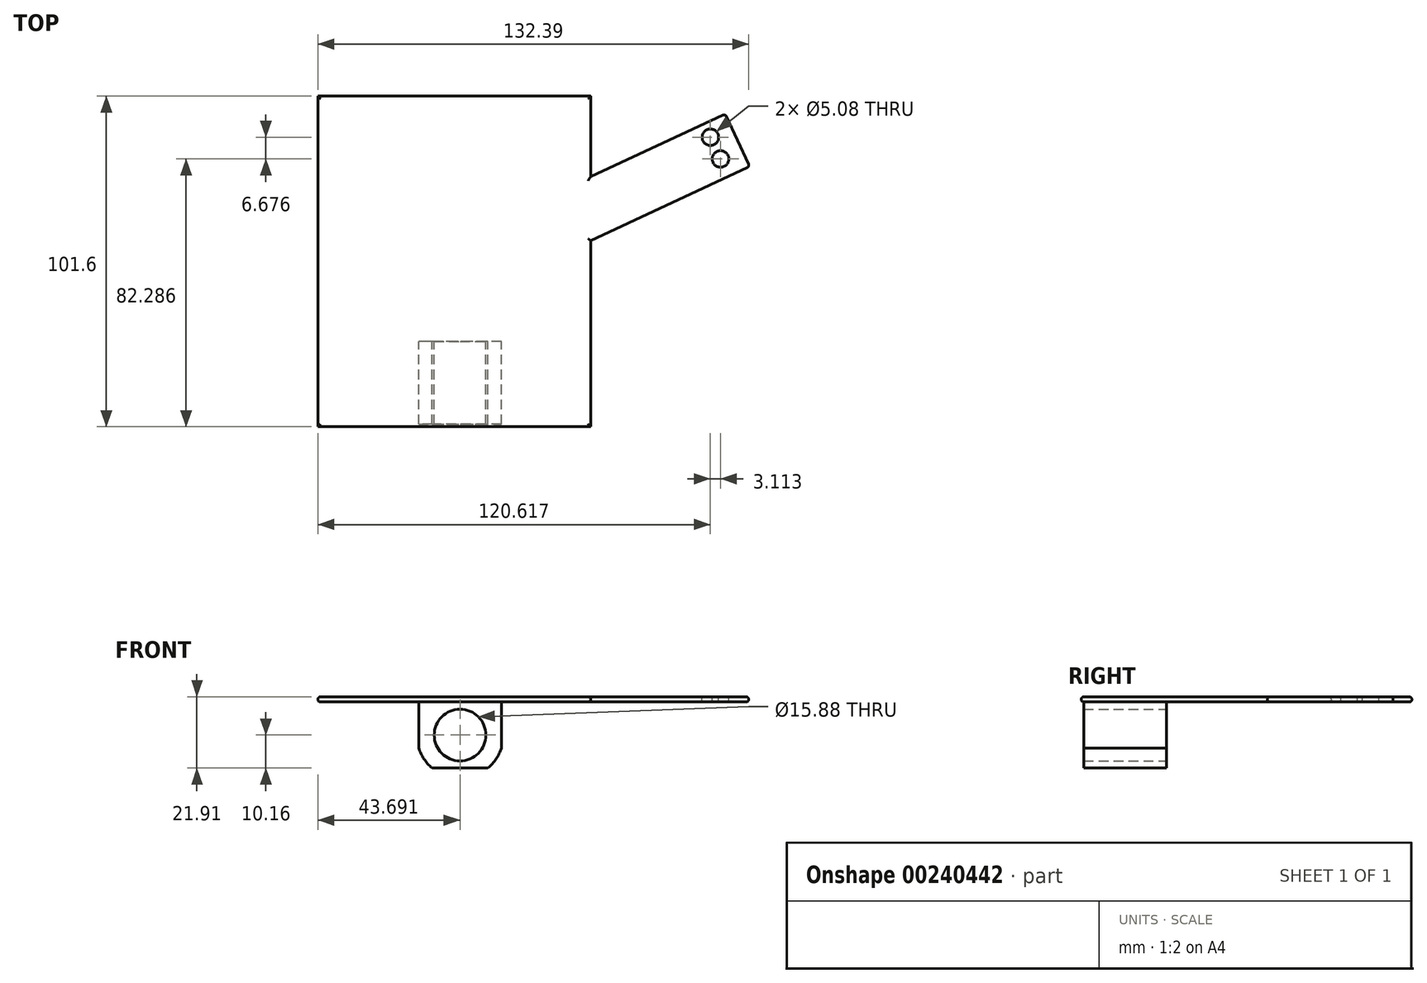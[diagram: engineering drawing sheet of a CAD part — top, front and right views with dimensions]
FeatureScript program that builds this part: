
annotation { "Feature Type Name" : "Feature", "Feature Type Description" : "" }
export const myFeature = defineFeature(function(context is Context, id is Id, definition is map)
    precondition{}
    {
        {
            var Q0;
            Q0=qCreatedBy(makeId("Top.planeOp"),FACE);
            var sketch = newSketch(context, id + "F0", { "sketchPlane" : qUnion([Q0])});
            skLineSegment(sketch, "E0.bottom", {"start": v(-47.59, -30.35) * mm, "end": v(36.23, -30.35) * mm});
            skLineSegment(sketch, "E0.top", {"start": v(-47.59, 71.25) * mm, "end": v(36.23, 71.25) * mm});
            skLineSegment(sketch, "E0.left", {"start": v(-47.59, -30.35) * mm, "end": v(-47.59, 71.25) * mm});
            skLineSegment(sketch, "E0.right", {"start": v(36.23, -30.35) * mm, "end": v(36.23, 71.25) * mm});
            skLineSegment(sketch, "E1.bottom", {"start": v(-47.59, 71.25) * mm, "end": v(-34.89, 71.25) * mm});
            skLineSegment(sketch, "E1.top", {"start": v(-47.59, 122.05) * mm, "end": v(-34.89, 122.05) * mm});
            skLineSegment(sketch, "E1.left", {"start": v(-47.59, 71.25) * mm, "end": v(-47.59, 122.05) * mm});
            skLineSegment(sketch, "E1.right", {"start": v(-34.89, 71.25) * mm, "end": v(-34.89, 122.05) * mm});
            skLineSegment(sketch, "E2.bottom", {"start": v(-27.27, 71.25) * mm, "end": v(-13.3, 71.25) * mm});
            skLineSegment(sketch, "E2.top", {"start": v(-27.27, 134.75) * mm, "end": v(-13.3, 134.75) * mm});
            skLineSegment(sketch, "E2.left", {"start": v(-27.27, 71.25) * mm, "end": v(-27.27, 134.75) * mm});
            skLineSegment(sketch, "E2.right", {"start": v(-13.3, 71.25) * mm, "end": v(-13.3, 134.75) * mm});
            skLineSegment(sketch, "E3.bottom", {"start": v(-5.68, 71.25) * mm, "end": v(10.83, 71.25) * mm});
            skLineSegment(sketch, "E3.top", {"start": v(-5.68, 153.8) * mm, "end": v(10.83, 153.8) * mm});
            skLineSegment(sketch, "E3.left", {"start": v(-5.68, 71.25) * mm, "end": v(-5.68, 153.8) * mm});
            skLineSegment(sketch, "E3.right", {"start": v(10.83, 71.25) * mm, "end": v(10.83, 153.8) * mm});
            skLineSegment(sketch, "E4.bottom", {"start": v(21, 71.25) * mm, "end": v(36.23, 71.25) * mm});
            skLineSegment(sketch, "E4.top", {"start": v(21, 138.37) * mm, "end": v(36.23, 138.37) * mm});
            skLineSegment(sketch, "E4.left", {"start": v(21, 71.25) * mm, "end": v(21, 138.37) * mm});
            skLineSegment(sketch, "E4.right", {"start": v(36.23, 71.25) * mm, "end": v(36.23, 138.37) * mm});
            skLineSegment(sketch, "E5", {"start": v(36.23, 26.88) * mm, "end": v(85.05, 49.65) * mm});
            skLineSegment(sketch, "E6", {"start": v(85.05, 49.65) * mm, "end": v(77.54, 65.76) * mm});
            skLineSegment(sketch, "E7", {"start": v(77.54, 65.76) * mm, "end": v(36.23, 46.5) * mm});
            skLineSegment(sketch, "E8", {"start": v(36.23, 46.5) * mm, "end": v(36.23, 26.88) * mm});
            skSolve(sketch);
        }
        {
            var Q0;
            {var subQ3=sQuery(id+"F0.wireOp",EDGE,"E0.bottom");Q0=makeQuery(id+"F0.imprint","IMPRINT",FACE,{"disambiguationData":[TD([[makeQuery(id+"F0.imprint","IMPRINT",EDGE,{"derivedFrom":subQ3}),1.0]])]});}
            var Q1;
            Q1=makeQuery(id+"F0.imprint","IMPRINT",FACE,{"disambiguationData":[TD([[makeQuery(id+"F0.imprint","IMPRINT",EDGE,{"derivedFrom":sQuery(id+"F0.wireOp",EDGE,"E1.bottom")}),1.0]])]});
            var Q2;
            Q2=makeQuery(id+"F0.imprint","IMPRINT",FACE,{"disambiguationData":[TD([[makeQuery(id+"F0.imprint","IMPRINT",EDGE,{"derivedFrom":sQuery(id+"F0.wireOp",EDGE,"E2.bottom")}),1.0]])]});
            var Q3;
            Q3=makeQuery(id+"F0.imprint","IMPRINT",FACE,{"disambiguationData":[TD([[makeQuery(id+"F0.imprint","IMPRINT",EDGE,{"derivedFrom":sQuery(id+"F0.wireOp",EDGE,"E3.bottom")}),1.0]])]});
            var Q4;
            Q4=makeQuery(id+"F0.imprint","IMPRINT",FACE,{"disambiguationData":[TD([[makeQuery(id+"F0.imprint","IMPRINT",EDGE,{"derivedFrom":sQuery(id+"F0.wireOp",EDGE,"E4.bottom")}),1.0]])]});
            var Q5;
            Q5=makeQuery(id+"F0.imprint","IMPRINT",FACE,{"disambiguationData":[TD([[makeQuery(id+"F0.imprint","IMPRINT",EDGE,{"derivedFrom":sQuery(id+"F0.wireOp",EDGE,"E5")}),1.0]])]});
            extrude(context, id + "F1", {"entities" : qUnion([Q0, Q1, Q2, Q3, Q4, Q5]), "depth" : 1.59 * mm});
        }
        {
            var Q0;
            Q0=makeQuery(id+"F1.opExtrude","CAP_EDGE",EDGE,{"disambiguationData":[OSD([sQuery(id+"F0.wireOp",EDGE,"E1.top")])],"isStart":false});
            var Q1;
            Q1=makeQuery(id+"F1.opExtrude","CAP_EDGE",EDGE,{"disambiguationData":[OSD([sQuery(id+"F0.wireOp",EDGE,"E2.top")])],"isStart":false});
            var Q2;
            Q2=makeQuery(id+"F1.opExtrude","CAP_EDGE",EDGE,{"disambiguationData":[OSD([sQuery(id+"F0.wireOp",EDGE,"E3.top")])],"isStart":false});
            var Q3;
            Q3=makeQuery(id+"F1.opExtrude","CAP_EDGE",EDGE,{"disambiguationData":[OSD([sQuery(id+"F0.wireOp",EDGE,"E4.top")])],"isStart":false});
            var Q4;
            Q4=makeQuery(id+"F1.opExtrude","CAP_EDGE",EDGE,{"disambiguationData":[OSD([sQuery(id+"F0.wireOp",EDGE,"E6")])],"isStart":false});
            fillet(context, id + "F2", {"entities" : qUnion([Q0, Q1, Q2, Q3, Q4]), "radius" : 0.76 * mm, "tangentPropagation" : true, "allowEdgeOverflow" : false});
        }
        {
            var Q0;
            Q0=makeQuery(id+"F1.opExtrude","CAP_EDGE",EDGE,{"disambiguationData":[OSD([sQuery(id+"F0.wireOp",EDGE,"E6")])],"isStart":true});
            var Q1;
            Q1=makeQuery(id+"F1.opExtrude","CAP_EDGE",EDGE,{"disambiguationData":[OSD([sQuery(id+"F0.wireOp",EDGE,"E4.top")])],"isStart":true});
            var Q2;
            Q2=makeQuery(id+"F1.opExtrude","CAP_EDGE",EDGE,{"disambiguationData":[OSD([sQuery(id+"F0.wireOp",EDGE,"E3.top")])],"isStart":true});
            var Q3;
            Q3=makeQuery(id+"F1.opExtrude","CAP_EDGE",EDGE,{"disambiguationData":[OSD([sQuery(id+"F0.wireOp",EDGE,"E2.top")])],"isStart":true});
            var Q4;
            Q4=makeQuery(id+"F1.opExtrude","CAP_EDGE",EDGE,{"disambiguationData":[OSD([sQuery(id+"F0.wireOp",EDGE,"E1.top")])],"isStart":true});
            fillet(context, id + "F3", {"entities" : qUnion([Q0, Q1, Q2, Q3, Q4]), "radius" : 0.76 * mm, "tangentPropagation" : true, "allowEdgeOverflow" : false});
        }
        {
            var Q0;
            Q0=makeQuery(id+"F1.opExtrude","CAP_FACE",FACE,{"disambiguationData":[OSD([sQuery(id+"F0.wireOp",EDGE,"E0.bottom"),sQuery(id+"F0.wireOp",EDGE,"E0.top"),sQuery(id+"F0.wireOp",EDGE,"E0.left"),sQuery(id+"F0.wireOp",EDGE,"E0.right"),sQuery(id+"F0.wireOp",EDGE,"E1.top"),sQuery(id+"F0.wireOp",EDGE,"E1.left"),sQuery(id+"F0.wireOp",EDGE,"E1.right"),sQuery(id+"F0.wireOp",EDGE,"E2.top"),sQuery(id+"F0.wireOp",EDGE,"E2.left"),sQuery(id+"F0.wireOp",EDGE,"E2.right"),sQuery(id+"F0.wireOp",EDGE,"E3.top"),sQuery(id+"F0.wireOp",EDGE,"E3.left"),sQuery(id+"F0.wireOp",EDGE,"E3.right"),sQuery(id+"F0.wireOp",EDGE,"E4.top"),sQuery(id+"F0.wireOp",EDGE,"E4.left"),sQuery(id+"F0.wireOp",EDGE,"E4.right"),sQuery(id+"F0.wireOp",EDGE,"E5"),sQuery(id+"F0.wireOp",EDGE,"E6"),sQuery(id+"F0.wireOp",EDGE,"E7")])],"isStart":false});
            var Q1;
            Q1=makeQuery(id+"F1.opExtrude","CAP_FACE",FACE,{"disambiguationData":[OSD([sQuery(id+"F0.wireOp",EDGE,"E0.bottom"),sQuery(id+"F0.wireOp",EDGE,"E0.top"),sQuery(id+"F0.wireOp",EDGE,"E0.left"),sQuery(id+"F0.wireOp",EDGE,"E0.right"),sQuery(id+"F0.wireOp",EDGE,"E1.top"),sQuery(id+"F0.wireOp",EDGE,"E1.left"),sQuery(id+"F0.wireOp",EDGE,"E1.right"),sQuery(id+"F0.wireOp",EDGE,"E2.top"),sQuery(id+"F0.wireOp",EDGE,"E2.left"),sQuery(id+"F0.wireOp",EDGE,"E2.right"),sQuery(id+"F0.wireOp",EDGE,"E3.top"),sQuery(id+"F0.wireOp",EDGE,"E3.left"),sQuery(id+"F0.wireOp",EDGE,"E3.right"),sQuery(id+"F0.wireOp",EDGE,"E4.top"),sQuery(id+"F0.wireOp",EDGE,"E4.left"),sQuery(id+"F0.wireOp",EDGE,"E4.right"),sQuery(id+"F0.wireOp",EDGE,"E5"),sQuery(id+"F0.wireOp",EDGE,"E6"),sQuery(id+"F0.wireOp",EDGE,"E7")])],"isStart":true});
            fillet(context, id + "F4", {"entities" : qUnion([Q0, Q1]), "radius" : 0.76 * mm, "tangentPropagation" : true, "allowEdgeOverflow" : false});
        }
        {
            var Q0;
            Q0=makeQuery(id+"F1.opExtrude","CAP_FACE",FACE,{"disambiguationData":[OSD([sQuery(id+"F0.wireOp",EDGE,"E0.bottom"),sQuery(id+"F0.wireOp",EDGE,"E0.top"),sQuery(id+"F0.wireOp",EDGE,"E0.left"),sQuery(id+"F0.wireOp",EDGE,"E0.right"),sQuery(id+"F0.wireOp",EDGE,"E1.top"),sQuery(id+"F0.wireOp",EDGE,"E1.left"),sQuery(id+"F0.wireOp",EDGE,"E1.right"),sQuery(id+"F0.wireOp",EDGE,"E2.top"),sQuery(id+"F0.wireOp",EDGE,"E2.left"),sQuery(id+"F0.wireOp",EDGE,"E2.right"),sQuery(id+"F0.wireOp",EDGE,"E3.top"),sQuery(id+"F0.wireOp",EDGE,"E3.left"),sQuery(id+"F0.wireOp",EDGE,"E3.right"),sQuery(id+"F0.wireOp",EDGE,"E4.top"),sQuery(id+"F0.wireOp",EDGE,"E4.left"),sQuery(id+"F0.wireOp",EDGE,"E4.right"),sQuery(id+"F0.wireOp",EDGE,"E5"),sQuery(id+"F0.wireOp",EDGE,"E6"),sQuery(id+"F0.wireOp",EDGE,"E7")])],"isStart":false});
            var sketch = newSketch(context, id + "F5", { "sketchPlane" : qUnion([Q0])});
            skCircle(sketch, "E9", {"center": v(73.03, 58.61) * mm, "radius": 2.54 * mm});
            skCircle(sketch, "E10", {"center": v(76.14, 51.94) * mm, "radius": 2.54 * mm});
            skCircle(sketch, "E11", {"center": v(24.93, 133.8) * mm, "radius": 2.54 * mm});
            skCircle(sketch, "E12", {"center": v(32.3, 133.8) * mm, "radius": 2.54 * mm});
            skCircle(sketch, "E13", {"center": v(-1.74, 149.23) * mm, "radius": 2.54 * mm});
            skCircle(sketch, "E14", {"center": v(6.9, 149.23) * mm, "radius": 2.54 * mm});
            skCircle(sketch, "E15", {"center": v(-23.97, 130.18) * mm, "radius": 2.54 * mm});
            skCircle(sketch, "E16", {"center": v(-16.6, 130.18) * mm, "radius": 2.54 * mm});
            skCircle(sketch, "E17", {"center": v(-44.29, 117.48) * mm, "radius": 1.9 * mm});
            skCircle(sketch, "E18", {"center": v(-38.19, 117.48) * mm, "radius": 1.9 * mm});
            skSolve(sketch);
        }
        {
            var Q0;
            Q0 = qSketchRegion(id + "F5", true);
            extrude(context, id + "F6", {"entities" : qUnion([Q0]), "operationType" : NewBodyOperationType.REMOVE, "oppositeDirection" : true, "depth" : 25.4 * mm});
        }
        {
            var Q0;
            Q0=makeQuery(id+"F1.opExtrude","CAP_FACE",FACE,{"disambiguationData":[OSD([sQuery(id+"F0.wireOp",EDGE,"E0.bottom"),sQuery(id+"F0.wireOp",EDGE,"E0.top"),sQuery(id+"F0.wireOp",EDGE,"E0.left"),sQuery(id+"F0.wireOp",EDGE,"E0.right"),sQuery(id+"F0.wireOp",EDGE,"E1.top"),sQuery(id+"F0.wireOp",EDGE,"E1.left"),sQuery(id+"F0.wireOp",EDGE,"E1.right"),sQuery(id+"F0.wireOp",EDGE,"E2.top"),sQuery(id+"F0.wireOp",EDGE,"E2.left"),sQuery(id+"F0.wireOp",EDGE,"E2.right"),sQuery(id+"F0.wireOp",EDGE,"E3.top"),sQuery(id+"F0.wireOp",EDGE,"E3.left"),sQuery(id+"F0.wireOp",EDGE,"E3.right"),sQuery(id+"F0.wireOp",EDGE,"E4.top"),sQuery(id+"F0.wireOp",EDGE,"E4.left"),sQuery(id+"F0.wireOp",EDGE,"E4.right"),sQuery(id+"F0.wireOp",EDGE,"E5"),sQuery(id+"F0.wireOp",EDGE,"E6"),sQuery(id+"F0.wireOp",EDGE,"E7")])],"isStart":true});
            var sketch = newSketch(context, id + "F7", { "sketchPlane" : qUnion([Q0])});
            skLineSegment(sketch, "E19.bottom", {"start": v(8.8, 29.6) * mm, "end": v(-16.6, 29.6) * mm});
            skLineSegment(sketch, "E19.top", {"start": v(8.8, 4.2) * mm, "end": v(-16.6, 4.2) * mm});
            skLineSegment(sketch, "E19.left", {"start": v(8.8, 29.6) * mm, "end": v(8.8, 4.2) * mm});
            skLineSegment(sketch, "E19.right", {"start": v(-16.6, 29.6) * mm, "end": v(-16.6, 4.2) * mm});
            skSolve(sketch);
        }
        {
            var Q0;
            Q0 = qSketchRegion(id + "F7", true);
            extrude(context, id + "F8", {"entities" : qUnion([Q0]), "operationType" : NewBodyOperationType.ADD, "depth" : 20.32 * mm});
        }
        {
            var Q0;
            Q0=makeQuery(id+"F8.opExtrude","SWEPT_FACE",FACE,{"disambiguationData":[OSD([sQuery(id+"F7.wireOp",EDGE,"E19.top")])]});
            var sketch = newSketch(context, id + "F9", { "sketchPlane" : qUnion([Q0])});
            skCircle(sketch, "E20", {"center": v(3.9, -10.16) * mm, "radius": 7.94 * mm});
            skSolve(sketch);
        }
        {
            var Q0;
            Q0 = qSketchRegion(id + "F9", true);
            extrude(context, id + "F10", {"entities" : qUnion([Q0]), "operationType" : NewBodyOperationType.REMOVE, "oppositeDirection" : true, "depth" : 25.4 * mm});
        }
        {
            var Q0;
            Q0=makeQuery(id+"F8.opExtrude","SWEPT_FACE",FACE,{"disambiguationData":[OSD([sQuery(id+"F7.wireOp",EDGE,"E19.top")])]});
            var sketch = newSketch(context, id + "F11", { "sketchPlane" : qUnion([Q0])});
            skCircle(sketch, "E21", {"center": v(3.9, -10.16) * mm, "radius": 13.3 * mm});
            skSolve(sketch);
        }
        {
            var Q0;
            {var subQ0=sQuery(id+"F11.wireOp",EDGE,"E21");var subQ1=sQuery(id+"F7.wireOp",EDGE,"E19.top");var subQ2=makeQuery(id+"F8.opExtrude","CAP_EDGE",EDGE,{"disambiguationData":[OSD([subQ1])],"isStart":false});var subQ3=makeQuery(id+"F11.imprint","INTERSECT",VERTEX,{"disambiguationData":[OD(1.0)],"derivedFrom":[subQ2,subQ0]});Q0=makeQuery(id+"F11.imprint","IMPRINT",FACE,{"disambiguationData":[TD([[makeQuery(id+"F11.imprint","IMPRINT",EDGE,{"disambiguationData":[TD([[subQ3,-1.0]])],"derivedFrom":subQ0}),-1.0]])]});}
            var Q1;
            {var subQ0=sQuery(id+"F11.wireOp",EDGE,"E21");var subQ1=sQuery(id+"F7.wireOp",EDGE,"E19.top");var subQ4=makeQuery(id+"F8.opExtrude","CAP_EDGE",EDGE,{"disambiguationData":[OSD([subQ1])],"isStart":false});var subQ5=makeQuery(id+"F11.imprint","INTERSECT",VERTEX,{"disambiguationData":[OD(0.0)],"derivedFrom":[subQ4,subQ0]});Q1=makeQuery(id+"F11.imprint","IMPRINT",FACE,{"disambiguationData":[TD([[makeQuery(id+"F11.imprint","IMPRINT",EDGE,{"disambiguationData":[TD([[subQ5,1.0]])],"derivedFrom":subQ0}),-1.0]])]});}
            extrude(context, id + "F12", {"entities" : qUnion([Q0, Q1]), "operationType" : NewBodyOperationType.REMOVE, "oppositeDirection" : true, "depth" : 25.4 * mm});
        }
    });
